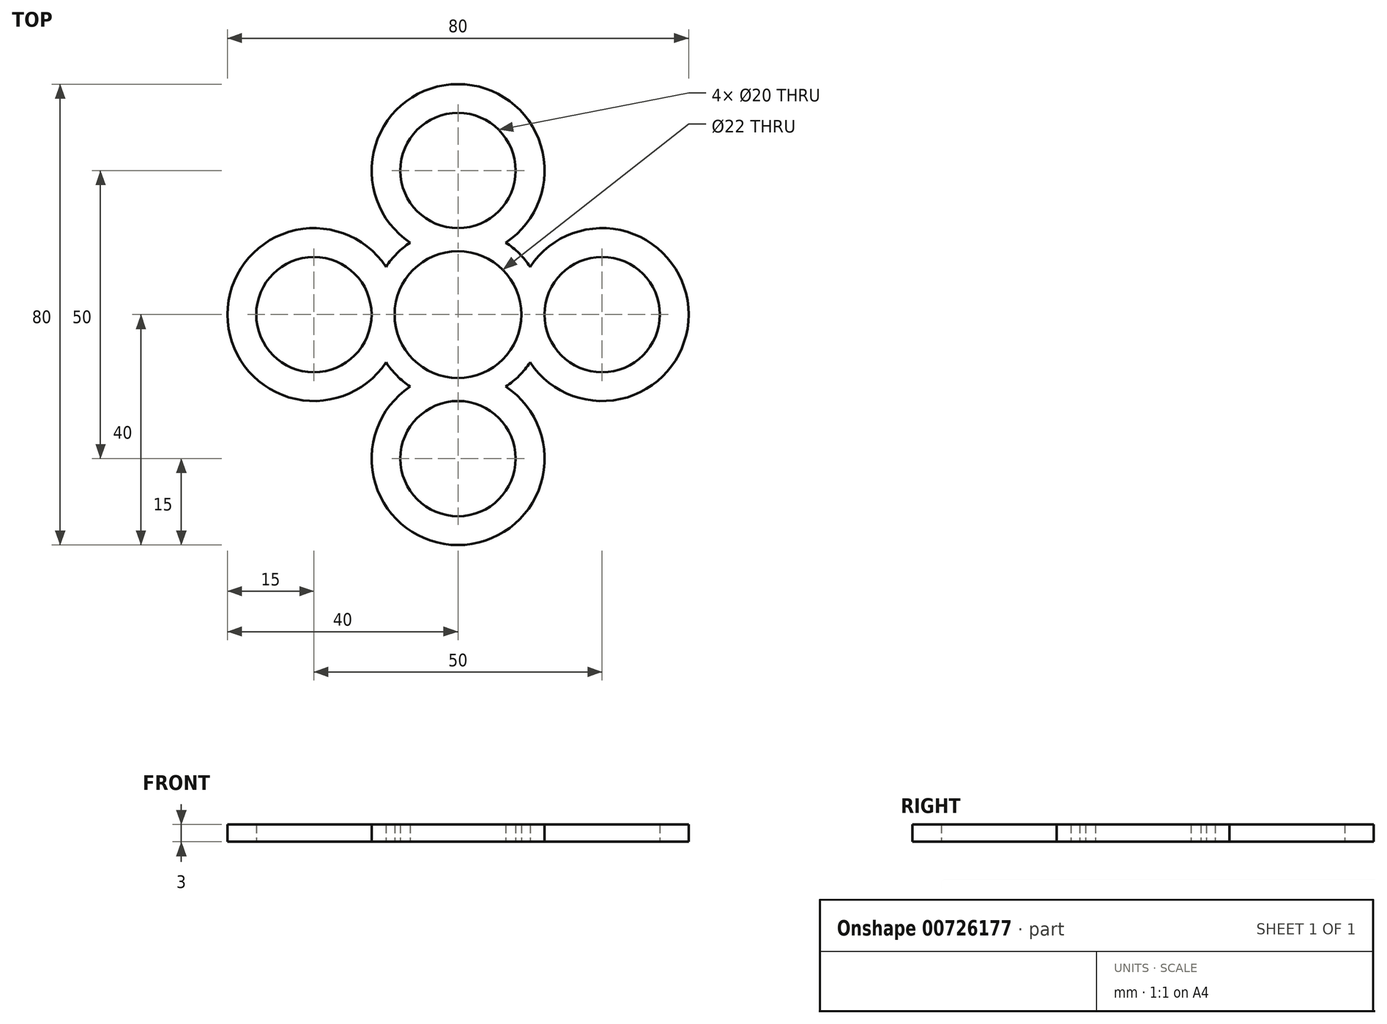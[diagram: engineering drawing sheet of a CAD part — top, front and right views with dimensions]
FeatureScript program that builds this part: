
annotation { "Feature Type Name" : "Feature", "Feature Type Description" : "" }
export const myFeature = defineFeature(function(context is Context, id is Id, definition is map)
    precondition{}
    {
        {
            var Q0;
            Q0=qCreatedBy(makeId("Top.planeOp"),FACE);
            var sketch = newSketch(context, id + "F0", { "sketchPlane" : qUnion([Q0])});
            skArc(sketch, "E0", {"start": v(11, 0) * mm, "mid": v(0, 11) * mm, "end": v(-11, 0) * mm});
            skArc(sketch, "E1", {"start": v(-8.3, 12.5) * mm, "mid": v(-10.6, 10.6) * mm, "end": v(-12.5, 8.3) * mm});
            skLineSegment(sketch, "E2", {"start": v(0, 0) * mm, "end": v(0, 25) * mm});
            skCircle(sketch, "E3", {"center": v(0, 25) * mm, "radius": 10 * mm});
            skArc(sketch, "E4", {"start": v(8.3, 12.5) * mm, "mid": v(0, 40) * mm, "end": v(-8.3, 12.5) * mm});
            skLineSegment(sketch, "E5", {"start": v(35, 0) * mm, "end": v(35.36, 0) * mm});
            skArc(sketch, "E6.trimOffspring", {"start": v(12.5, 8.3) * mm, "mid": v(10.6, 10.6) * mm, "end": v(8.3, 12.5) * mm});
            skCircle(sketch, "E7.1.0", {"center": v(-25, 0) * mm, "radius": 10 * mm});
            skArc(sketch, "E7.1.1", {"start": v(-12.5, 8.3) * mm, "mid": v(-40, 0) * mm, "end": v(-12.5, -8.3) * mm});
            skArc(sketch, "E7.1.3", {"start": v(0, 11) * mm, "mid": v(-11, 0) * mm, "end": v(0, -11) * mm});
            skCircle(sketch, "E7.2.0", {"center": v(0, -25) * mm, "radius": 10 * mm});
            skArc(sketch, "E7.2.1", {"start": v(-8.3, -12.5) * mm, "mid": v(0, -40) * mm, "end": v(8.3, -12.5) * mm});
            skArc(sketch, "E7.2.2", {"start": v(-12.5, -8.3) * mm, "mid": v(-10.6, -10.6) * mm, "end": v(-8.3, -12.5) * mm});
            skArc(sketch, "E7.2.3", {"start": v(-11, 0) * mm, "mid": v(0, -11) * mm, "end": v(11, 0) * mm});
            skCircle(sketch, "E7.3.0", {"center": v(25, 0) * mm, "radius": 10 * mm});
            skArc(sketch, "E7.3.1", {"start": v(12.5, -8.3) * mm, "mid": v(40, 0) * mm, "end": v(12.5, 8.3) * mm});
            skArc(sketch, "E7.3.2", {"start": v(8.3, -12.5) * mm, "mid": v(10.6, -10.6) * mm, "end": v(12.5, -8.3) * mm});
            skArc(sketch, "E7.3.3", {"start": v(0, -11) * mm, "mid": v(11, 0) * mm, "end": v(0, 11) * mm});
            skPoint(sketch, "E8.orphan", {"position": v(0, 15) * mm});
            skPoint(sketch, "E9.orphan", {"position": v(15, 0) * mm});
            skPoint(sketch, "E10.orphan", {"position": v(-15, 0) * mm});
            skPoint(sketch, "E11.orphan", {"position": v(0, -15) * mm});
            skPoint(sketch, "E12.orphan", {"position": v(-24.5, 0) * mm});
            skSolve(sketch);
        }
        {
            var Q0;
            Q0 = qSketchRegion(id + "F0", true);
            extrude(context, id + "F1", {"entities" : qUnion([Q0]), "depth" : 3 * mm, "offsetDistance" : 25 * mm});
        }
    });
